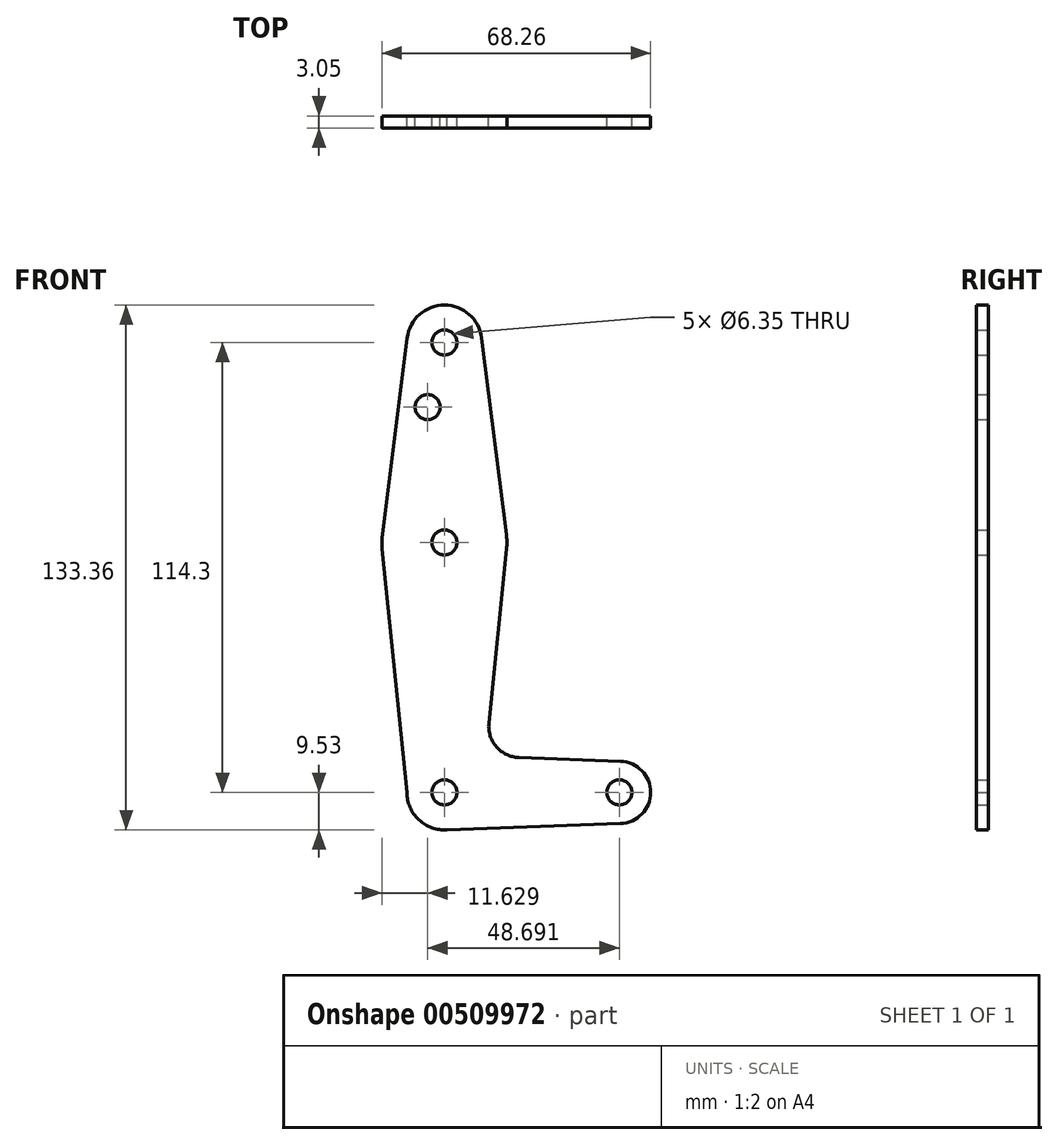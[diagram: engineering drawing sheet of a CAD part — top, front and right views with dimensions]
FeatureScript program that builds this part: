
annotation { "Feature Type Name" : "Feature", "Feature Type Description" : "" }
export const myFeature = defineFeature(function(context is Context, id is Id, definition is map)
    precondition{}
    {
        {
            var Q0;
            Q0=qCreatedBy(makeId("Front.planeOp"),FACE);
            var sketch = newSketch(context, id + "F0", { "sketchPlane" : qUnion([Q0])});
            skLineSegment(sketch, "E0", {"start": v(0, 0) * mm, "end": v(44.45, 0) * mm, "construction": true});
            skCircle(sketch, "E1", {"center": v(0, 0) * mm, "radius": 9.53 * mm});
            skCircle(sketch, "E2", {"center": v(44.45, 0) * mm, "radius": 7.94 * mm});
            skLineSegment(sketch, "E3", {"start": v(0, -9.52) * mm, "end": v(44.73, -7.93) * mm});
            skLineSegment(sketch, "E4", {"start": v(44.73, 7.93) * mm, "end": v(18.93, 8.85) * mm});
            skLineSegment(sketch, "E5", {"start": v(0, 114.3) * mm, "end": v(0, 0) * mm, "construction": true});
            skCircle(sketch, "E6", {"center": v(0, 114.3) * mm, "radius": 9.53 * mm});
            skCircle(sketch, "E7", {"center": v(0, 63.5) * mm, "radius": 15.88 * mm});
            skLineSegment(sketch, "E8", {"start": v(-15.8, 61.9) * mm, "end": v(-9.52, 0) * mm});
            skLineSegment(sketch, "E9", {"start": v(15.8, 61.9) * mm, "end": v(11.3, 17.6) * mm});
            skLineSegment(sketch, "E10", {"start": v(-15.75, 65.48) * mm, "end": v(-9.45, 115.5) * mm});
            skLineSegment(sketch, "E11", {"start": v(15.75, 65.48) * mm, "end": v(9.45, 115.5) * mm});
            skCircle(sketch, "E12", {"center": v(0, 114.3) * mm, "radius": 3.18 * mm});
            skCircle(sketch, "E13", {"center": v(0, 63.5) * mm, "radius": 3.18 * mm});
            skCircle(sketch, "E14", {"center": v(0, 0) * mm, "radius": 3.18 * mm});
            skCircle(sketch, "E15", {"center": v(44.45, 0) * mm, "radius": 3.18 * mm});
            skCircle(sketch, "E16", {"center": v(-4.24, 97.87) * mm, "radius": 3.18 * mm});
            skArc(sketch, "E17.filletArc", {"start": v(11.3, 17.6) * mm, "mid": v(13.22, 11.57) * mm, "end": v(18.93, 8.85) * mm});
            skSolve(sketch);
        }
        {
            var Q0;
            Q0 = qSketchRegion(id + "F0", true);
            extrude(context, id + "F1", {"entities" : qUnion([Q0]), "depth" : 3.05 * mm, "offsetDistance" : 25.4 * mm});
        }
    });
